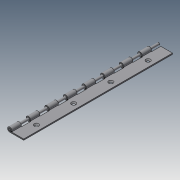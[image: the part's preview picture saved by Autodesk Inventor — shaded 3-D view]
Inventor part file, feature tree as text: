
AUTODESK INVENTOR PART (.ipt)
format: ipt  version: 2018.3 (Build 223284000, 284)  size: 427,520 bytes
history: native  units: in
note: dims shown in document units (in); Inventor stores cm internally (conversion verified against a paired STEP export)
features: extrude x1, sketch x1, chamfer x1, other x1, mirror x1
ambient origin geometry x8: Origin, YZ Plane, XZ Plane, XY Plane, X Axis, Y Axis, Z Axis, Center Point
bodies: Solid1 (feature_tree), Solid2 (feature_tree), Solid3 (feature_tree)
feature tree (5):
  extrude  "Extrusion1"  Depth=4.0in
  sketch  "Sketch1"  dims[d0=4.0in d1=4.0in d2=1.0in d3=0.0in]
  chamfer  "Chamfer1"  Distance=1.0in
  other  "LPattern4"
  mirror  "Mirror3"
